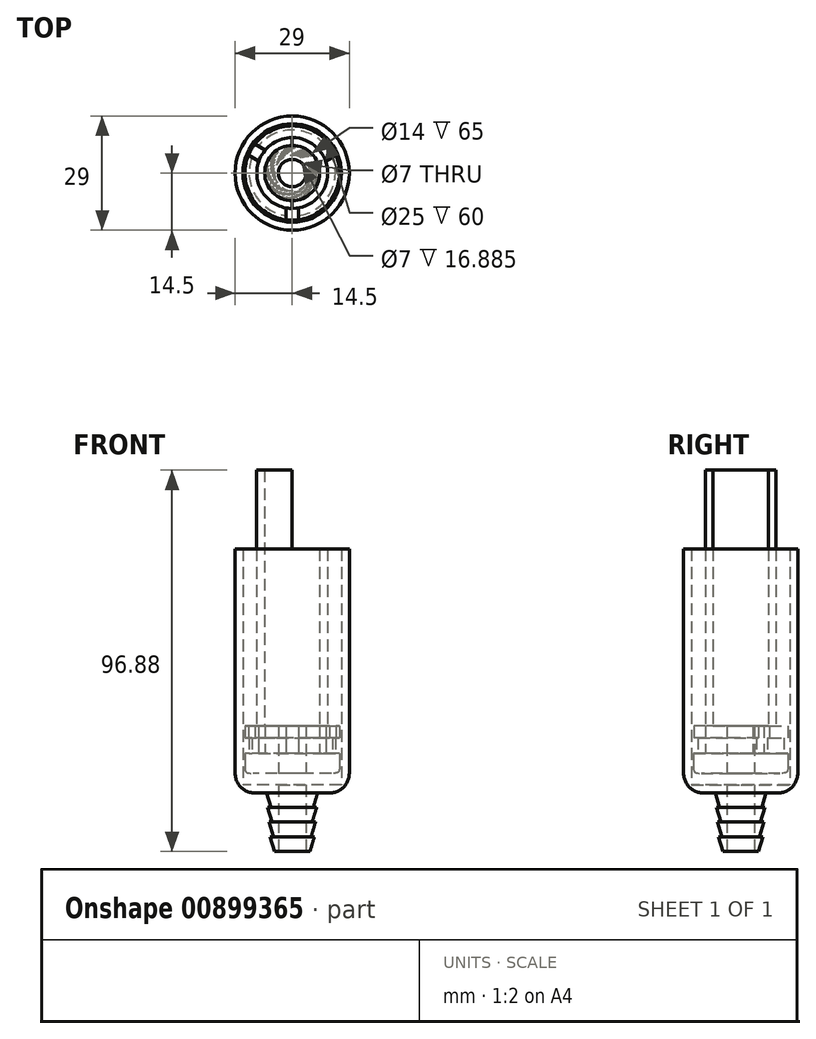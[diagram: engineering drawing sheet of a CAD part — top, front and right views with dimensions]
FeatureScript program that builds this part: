
annotation { "Feature Type Name" : "Feature", "Feature Type Description" : "" }
export const myFeature = defineFeature(function(context is Context, id is Id, definition is map)
    precondition{}
    {
        {
            var Q0;
            Q0=qCreatedBy(makeId("Top.planeOp"),FACE);
            var sketch = newSketch(context, id + "F0", { "sketchPlane" : qUnion([Q0])});
            skCircle(sketch, "E0", {"center": v(0, 0) * mm, "radius": 12 * mm});
            skSolve(sketch);
        }
        {
            var Q0;
            Q0=makeQuery(id+"F0.imprint","IMPRINT",FACE,{"disambiguationData":[TD([[makeQuery(id+"F0.imprint","IMPRINT",EDGE,{"derivedFrom":sQuery(id+"F0.wireOp",EDGE,"E0")}),1.0]])]});
            extrude(context, id + "F1", {"entities" : qUnion([Q0]), "depth" : 12 * mm, "offsetDistance" : 25 * mm});
        }
        {
            var Q0;
            Q0=makeQuery(id+"F1.opExtrude","CAP_FACE",FACE,{"disambiguationData":[OSD([sQuery(id+"F0.wireOp",EDGE,"E0")])],"isStart":false});
            var sketch = newSketch(context, id + "F2", { "sketchPlane" : qUnion([Q0])});
            skCircle(sketch, "E1", {"center": v(0, 0) * mm, "radius": 9 * mm});
            skCircle(sketch, "E2", {"center": v(0, 0) * mm, "radius": 7 * mm});
            skSolve(sketch);
        }
        {
            var Q0;
            Q0=makeQuery(id+"F2.imprint","IMPRINT",FACE,{"disambiguationData":[TD([[makeQuery(id+"F2.imprint","IMPRINT",EDGE,{"derivedFrom":sQuery(id+"F2.wireOp",EDGE,"E1")}),1.0]])]});
            extrude(context, id + "F3", {"entities" : qUnion([Q0]), "operationType" : NewBodyOperationType.ADD, "depth" : 65 * mm, "offsetDistance" : 25 * mm});
        }
        {
            var Q0;
            Q0=makeQuery(id+"F1.opExtrude","CAP_FACE",FACE,{"disambiguationData":[OSD([sQuery(id+"F0.wireOp",EDGE,"E0")])],"isStart":true});
            var sketch = newSketch(context, id + "F4", { "sketchPlane" : qUnion([Q0])});
            skLineSegment(sketch, "E3", {"start": v(8.06, 12) * mm, "end": v(-8.04, 12) * mm, "construction": true});
            skLineSegment(sketch, "E4", {"start": v(1.62, 8.93) * mm, "end": v(-1.62, 8.93) * mm});
            skPoint(sketch, "E5", {"position": v(0, 8.93) * mm});
            skLineSegment(sketch, "E6", {"start": v(1.62, 8.93) * mm, "end": v(1.62, 10.83) * mm});
            skLineSegment(sketch, "E7", {"start": v(-1.62, 8.93) * mm, "end": v(-1.62, 10.83) * mm});
            skLineSegment(sketch, "E8.1.0", {"start": v(-8.55, -3.06) * mm, "end": v(-6.92, -5.87) * mm});
            skPoint(sketch, "E8.1.1", {"position": v(-7.74, -4.47) * mm});
            skLineSegment(sketch, "E8.1.2", {"start": v(-6.92, -5.87) * mm, "end": v(-8.57, -6.82) * mm});
            skLineSegment(sketch, "E8.1.3", {"start": v(-8.55, -3.06) * mm, "end": v(-10.2, -4.01) * mm});
            skLineSegment(sketch, "E8.2.0", {"start": v(6.92, -5.87) * mm, "end": v(8.55, -3.06) * mm});
            skPoint(sketch, "E8.2.1", {"position": v(7.74, -4.47) * mm});
            skLineSegment(sketch, "E8.2.2", {"start": v(8.55, -3.06) * mm, "end": v(10.2, -4.01) * mm});
            skLineSegment(sketch, "E8.2.3", {"start": v(6.92, -5.87) * mm, "end": v(8.57, -6.82) * mm});
            skPoint(sketch, "E8.center", {"position": v(0, 0) * mm});
            skLineSegment(sketch, "E9", {"start": v(1.62, 10.83) * mm, "end": v(1.62, 10.83) * mm});
            skArc(sketch, "E10", {"start": v(-1.62, 10.83) * mm, "mid": v(0, -10.95) * mm, "end": v(1.62, 10.83) * mm});
            skArc(sketch, "E11", {"start": v(1.62, 10.83) * mm, "mid": v(0, 10.95) * mm, "end": v(-1.62, 10.83) * mm});
            skLineSegment(sketch, "E12", {"start": v(1.62, 10.83) * mm, "end": v(1.62, 11.89) * mm, "construction": true});
            skLineSegment(sketch, "E13", {"start": v(-1.62, 10.83) * mm, "end": v(-1.62, 11.89) * mm, "construction": true});
            skSolve(sketch);
        }
        {
            var Q0;
            Q0=makeQuery(id+"F4.imprint","IMPRINT",FACE,{"disambiguationData":[TD([[makeQuery(id+"F4.imprint","IMPRINT",EDGE,{"derivedFrom":makeQuery(id+"F1.opExtrude","CAP_EDGE",EDGE,{"disambiguationData":[OSD([sQuery(id+"F0.wireOp",EDGE,"E0")])],"isStart":true})}),-1.0]])]});
            extrude(context, id + "F5", {"entities" : qUnion([Q0]), "operationType" : NewBodyOperationType.REMOVE, "oppositeDirection" : true, "depth" : 9 * mm, "offsetDistance" : 25 * mm, "hasSecondDirection" : true, "secondDirectionOppositeDirection" : false, "secondDirectionDepth" : -5 * mm});
        }
        {
            var Q0;
            Q0=makeQuery(id+"F4.imprint","IMPRINT",FACE,{"disambiguationData":[TD([[makeQuery(id+"F4.imprint","IMPRINT",EDGE,{"derivedFrom":sQuery(id+"F4.wireOp",EDGE,"E4")}),-1.0]])]});
            var Q1;
            Q1=makeQuery(id+"F4.imprint","IMPRINT",FACE,{"disambiguationData":[TD([[makeQuery(id+"F4.imprint","IMPRINT",EDGE,{"derivedFrom":sQuery(id+"F4.wireOp",EDGE,"E8.1.0")}),-1.0]])]});
            var Q2;
            Q2=makeQuery(id+"F4.imprint","IMPRINT",FACE,{"disambiguationData":[TD([[makeQuery(id+"F4.imprint","IMPRINT",EDGE,{"derivedFrom":sQuery(id+"F4.wireOp",EDGE,"E8.2.0")}),-1.0]])]});
            var Q3;
            Q3=makeQuery(id+"F5.boolean.opBoolean","COPY",FACE,{"derivedFrom":makeQuery(id+"F5.opExtrude","CAP_FACE",FACE,{"disambiguationData":[OSD([sQuery(id+"F0.wireOp",EDGE,"E0"),sQuery(id+"F4.wireOp",EDGE,"bE9oeRPU-8ZHk-j5FX-hGk3-XUl1ZEH3Kncf")])],"isStart":false})});
            extrude(context, id + "F6", {"entities" : qUnion([Q0, Q1, Q2]), "operationType" : NewBodyOperationType.REMOVE, "endBound" : BoundingType.UP_TO_SURFACE, "oppositeDirection" : true, "depth" : 25 * mm, "endBoundEntityFace" : qUnion([Q3]), "offsetDistance" : 5 * mm, "hasSecondDirection" : true, "secondDirectionOppositeDirection" : true, "secondDirectionDepth" : 5 * mm});
        }
        {
            var Q0;
            {var subQ0=sQuery(id+"F4.wireOp",EDGE,"E10");var subQ1=sQuery(id+"F4.wireOp",EDGE,"E11");Q0=makeQuery(id+"F6.boolean.opBoolean","MERGE",FACE,{"derivedFrom":[makeQuery(id+"F5.boolean.opBoolean","COPY",FACE,{"derivedFrom":makeQuery(id+"F5.opExtrude","CAP_FACE",FACE,{"disambiguationData":[OSD([sQuery(id+"F0.wireOp",EDGE,"E0"),subQ0,subQ1])],"isStart":true})})],"fromTools":[makeQuery(id+"F6.opExtrude","CAP_FACE",FACE,{"disambiguationData":[OSD([sQuery(id+"F4.wireOp",EDGE,"E4"),sQuery(id+"F4.wireOp",EDGE,"E6"),sQuery(id+"F4.wireOp",EDGE,"E7"),subQ1])],"isStart":true}),makeQuery(id+"F6.opExtrude","CAP_FACE",FACE,{"disambiguationData":[OSD([sQuery(id+"F4.wireOp",EDGE,"E8.1.0"),sQuery(id+"F4.wireOp",EDGE,"E8.1.2"),sQuery(id+"F4.wireOp",EDGE,"E8.1.3"),subQ0])],"isStart":true}),makeQuery(id+"F6.opExtrude","CAP_FACE",FACE,{"disambiguationData":[OSD([sQuery(id+"F4.wireOp",EDGE,"E8.2.0"),sQuery(id+"F4.wireOp",EDGE,"E8.2.2"),sQuery(id+"F4.wireOp",EDGE,"E8.2.3"),subQ0])],"isStart":true})]});}
            var sketch = newSketch(context, id + "F7", { "sketchPlane" : qUnion([Q0])});
            skLineSegment(sketch, "E14", {"start": v(-1.62, -8.93) * mm, "end": v(-1.62, -11.89) * mm});
            skLineSegment(sketch, "E15", {"start": v(1.62, -8.93) * mm, "end": v(1.62, -11.89) * mm});
            skArc(sketch, "E16", {"start": v(-1.62, -11.89) * mm, "mid": v(0, -12) * mm, "end": v(1.62, -11.89) * mm});
            skPoint(sketch, "E17", {"position": v(0, -12) * mm});
            skPoint(sketch, "E18", {"position": v(0, -10.95) * mm});
            skLineSegment(sketch, "E19", {"start": v(1.62, -8.93) * mm, "end": v(-1.62, -8.93) * mm});
            skLineSegment(sketch, "E20.1.0", {"start": v(8.55, 3.06) * mm, "end": v(11.1, 4.54) * mm});
            skLineSegment(sketch, "E20.1.1", {"start": v(6.92, 5.87) * mm, "end": v(9.49, 7.35) * mm});
            skLineSegment(sketch, "E20.1.2", {"start": v(6.92, 5.87) * mm, "end": v(8.55, 3.06) * mm});
            skArc(sketch, "E20.1.3", {"start": v(11.1, 4.54) * mm, "mid": v(10.4, 6) * mm, "end": v(9.49, 7.35) * mm});
            skLineSegment(sketch, "E20.2.0", {"start": v(-6.92, 5.87) * mm, "end": v(-9.49, 7.35) * mm});
            skLineSegment(sketch, "E20.2.1", {"start": v(-8.55, 3.06) * mm, "end": v(-11.1, 4.54) * mm});
            skLineSegment(sketch, "E20.2.2", {"start": v(-8.55, 3.06) * mm, "end": v(-6.92, 5.87) * mm});
            skArc(sketch, "E20.2.3", {"start": v(-9.49, 7.35) * mm, "mid": v(-10.4, 6) * mm, "end": v(-11.1, 4.54) * mm});
            skSolve(sketch);
        }
        {
            var Q0;
            {var subQ15=sQuery(id+"F7.wireOp",EDGE,"E16");Q0=makeQuery(id+"F7.imprint","IMPRINT",FACE,{"disambiguationData":[TD([[makeQuery(id+"F7.imprint","IMPRINT",EDGE,{"derivedFrom":subQ15}),1.0]])]});}
            var Q1;
            {var subQ17=sQuery(id+"F7.wireOp",EDGE,"E20.2.2");Q1=makeQuery(id+"F7.imprint","IMPRINT",FACE,{"disambiguationData":[TD([[makeQuery(id+"F7.imprint","IMPRINT",EDGE,{"derivedFrom":subQ17}),1.0]])]});}
            var Q2;
            {var subQ17=sQuery(id+"F7.wireOp",EDGE,"E20.1.2");Q2=makeQuery(id+"F7.imprint","IMPRINT",FACE,{"disambiguationData":[TD([[makeQuery(id+"F7.imprint","IMPRINT",EDGE,{"derivedFrom":subQ17}),1.0]])]});}
            var Q3;
            {var subQ0=sQuery(id+"F0.wireOp",EDGE,"E0");Q3=makeQuery(id+"F3.boolean.opBoolean","SPLIT",FACE,{"disambiguationData":[TD([makeQuery(id+"F1.opExtrude","SWEPT_FACE",FACE,{"disambiguationData":[OSD([subQ0])]})])],"derivedFrom":makeQuery(id+"F1.opExtrude","CAP_FACE",FACE,{"disambiguationData":[OSD([subQ0])],"isStart":false})});}
            extrude(context, id + "F8", {"entities" : qUnion([Q0, Q1, Q2]), "operationType" : NewBodyOperationType.REMOVE, "endBound" : BoundingType.UP_TO_SURFACE, "depth" : 25 * mm, "endBoundEntityFace" : qUnion([Q3]), "offsetDistance" : 25 * mm});
        }
        {
            var Q0;
            Q0=makeQuery(id+"F1.opExtrude","CAP_EDGE",EDGE,{"disambiguationData":[OSD([sQuery(id+"F0.wireOp",EDGE,"E0")])],"isStart":true});
            fillet(context, id + "F9", {"entities" : qUnion([Q0]), "radius" : 2 * mm, "tangentPropagation" : true, "rho" : 0.7, "crossSection" : FilletCrossSection.CONIC, "allowEdgeOverflow" : false});
        }
        {
            var Q0;
            Q0=makeQuery(id+"F3.opExtrude","CAP_FACE",FACE,{"disambiguationData":[OSD([sQuery(id+"F2.wireOp",EDGE,"E1"),sQuery(id+"F2.wireOp",EDGE,"E2")])],"isStart":false});
            var sketch = newSketch(context, id + "F10", { "sketchPlane" : qUnion([Q0])});
            skLineSegment(sketch, "E21", {"start": v(0, 7) * mm, "end": v(0, 9) * mm});
            skLineSegment(sketch, "E22", {"start": v(0, -7) * mm, "end": v(0, -9) * mm});
            skArc(sketch, "E23", {"start": v(0, -7) * mm, "mid": v(7, 0) * mm, "end": v(0, 7) * mm});
            skArc(sketch, "E24", {"start": v(0, -9) * mm, "mid": v(9, 0) * mm, "end": v(0, 9) * mm});
            skSolve(sketch);
        }
        {
            var Q0;
            Q0=makeQuery(id+"F10.imprint","IMPRINT",FACE,{"disambiguationData":[TD([[makeQuery(id+"F10.imprint","IMPRINT",EDGE,{"derivedFrom":sQuery(id+"F10.wireOp",EDGE,"E21")}),-1.0]])]});
            extrude(context, id + "F11", {"entities" : qUnion([Q0]), "operationType" : NewBodyOperationType.REMOVE, "oppositeDirection" : true, "depth" : 20 * mm, "offsetDistance" : 25 * mm});
        }
        {
            var Q0;
            Q0=qCreatedBy(makeId("Top.planeOp"),FACE);
            var sketch = newSketch(context, id + "F12", { "sketchPlane" : qUnion([Q0])});
            skCircle(sketch, "E25.0", {"center": v(0, 0) * mm, "radius": 12 * mm, "construction": true});
            skCircle(sketch, "E26.0", {"center": v(0, 0) * mm, "radius": 12.5 * mm});
            skCircle(sketch, "E27.0", {"center": v(0, 0) * mm, "radius": 14.5 * mm});
            skSolve(sketch);
        }
        {
            var Q0;
            Q0=makeQuery(id+"F12.imprint","IMPRINT",FACE,{"disambiguationData":[TD([[makeQuery(id+"F12.imprint","IMPRINT",EDGE,{"derivedFrom":sQuery(id+"F12.wireOp",EDGE,"E26.0")}),-1.0]])]});
            var Q1;
            Q1=makeQuery(id+"F11.boolean.opBoolean","COPY",FACE,{"derivedFrom":makeQuery(id+"F11.opExtrude","CAP_FACE",FACE,{"disambiguationData":[OSD([sQuery(id+"F10.wireOp",EDGE,"E21"),sQuery(id+"F10.wireOp",EDGE,"E22"),sQuery(id+"F10.wireOp",EDGE,"E23"),sQuery(id+"F10.wireOp",EDGE,"E24")])],"isStart":false})});
            extrude(context, id + "F13", {"entities" : qUnion([Q0]), "endBound" : BoundingType.UP_TO_SURFACE, "depth" : 50 * mm, "endBoundEntityFace" : qUnion([Q1]), "offsetDistance" : 25 * mm, "hasSecondDirection" : true, "secondDirectionOppositeDirection" : true, "secondDirectionDepth" : 5 * mm});
        }
        {
            var Q0;
            Q0=makeQuery(id+"F13.opExtrude","CAP_FACE",FACE,{"disambiguationData":[OSD([sQuery(id+"F12.wireOp",EDGE,"E26.0"),sQuery(id+"F12.wireOp",EDGE,"E27.0")])],"isStart":true});
            var sketch = newSketch(context, id + "F14", { "sketchPlane" : qUnion([Q0])});
            skCircle(sketch, "E28.0", {"center": v(0, 0) * mm, "radius": 12.5 * mm});
            skSolve(sketch);
        }
        {
            var Q0;
            Q0=makeQuery(id+"F14.imprint","IMPRINT",FACE,{"disambiguationData":[TD([[makeQuery(id+"F14.imprint","IMPRINT",EDGE,{"derivedFrom":sQuery(id+"F14.wireOp",EDGE,"E28.0")}),-1.0]])]});
            extrude(context, id + "F15", {"entities" : qUnion([Q0]), "operationType" : NewBodyOperationType.ADD, "oppositeDirection" : true, "depth" : 2 * mm, "offsetDistance" : 25 * mm});
        }
        {
            var Q0;
            Q0=makeQuery(id+"F15.boolean.opBoolean","MERGE",FACE,{"derivedFrom":[makeQuery(id+"F13.opExtrude","CAP_FACE",FACE,{"disambiguationData":[OSD([sQuery(id+"F12.wireOp",EDGE,"E26.0"),sQuery(id+"F12.wireOp",EDGE,"E27.0")])],"isStart":true}),makeQuery(id+"F15.opExtrude","CAP_FACE",FACE,{"disambiguationData":[OSD([sQuery(id+"F14.wireOp",EDGE,"E28.0")])],"isStart":true})]});
            var sketch = newSketch(context, id + "F16", { "sketchPlane" : qUnion([Q0])});
            skCircle(sketch, "E29", {"center": v(0, 0) * mm, "radius": 3.5 * mm});
            skCircle(sketch, "E30.0", {"center": v(0, 0) * mm, "radius": 5.5 * mm});
            skSolve(sketch);
        }
        {
            var Q0;
            Q0=qCreatedBy(makeId("Right.planeOp"),FACE);
            var sketch = newSketch(context, id + "F17", { "sketchPlane" : qUnion([Q0])});
            skLineSegment(sketch, "E31", {"start": v(0, -4.88) * mm, "end": v(-6.5, -4.88) * mm});
            skLineSegment(sketch, "E32", {"start": v(-6.5, -4.88) * mm, "end": v(-5.35, -19.88) * mm, "construction": true});
            skLineSegment(sketch, "E33", {"start": v(-6.5, -4.88) * mm, "end": v(-5.36, -8.63) * mm});
            skLineSegment(sketch, "E34", {"start": v(-5.36, -8.63) * mm, "end": v(-6.21, -8.63) * mm});
            skLineSegment(sketch, "E35", {"start": v(-6.21, -8.63) * mm, "end": v(-5.07, -12.38) * mm});
            skLineSegment(sketch, "E36", {"start": v(-5.07, -12.38) * mm, "end": v(-5.93, -12.38) * mm});
            skLineSegment(sketch, "E37", {"start": v(-5.93, -12.38) * mm, "end": v(-4.79, -16.13) * mm});
            skLineSegment(sketch, "E38", {"start": v(-4.79, -16.13) * mm, "end": v(-5.64, -16.13) * mm});
            skLineSegment(sketch, "E39", {"start": v(-5.64, -16.13) * mm, "end": v(-4.5, -19.88) * mm});
            skLineSegment(sketch, "E40", {"start": v(-5.35, -19.88) * mm, "end": v(-4.5, -19.88) * mm, "construction": true});
            skLineSegment(sketch, "E41", {"start": v(0, -4.88) * mm, "end": v(0, -19.88) * mm});
            skLineSegment(sketch, "E42", {"start": v(-4.5, -19.88) * mm, "end": v(0, -19.88) * mm});
            skSolve(sketch);
        }
        {
            var Q0;
            Q0=makeQuery(id+"F17.imprint","IMPRINT",FACE,{"disambiguationData":[TD([[makeQuery(id+"F17.imprint","IMPRINT",EDGE,{"derivedFrom":sQuery(id+"F17.wireOp",EDGE,"E31")}),1.0]])]});
            var Q1;
            Q1=sQuery(id+"F17.wireOp",EDGE,"E41");
            revolve(context, id + "F18", {"operationType" : NewBodyOperationType.ADD, "surfaceOperationType" : NewSurfaceOperationType.NEW, "entities" : qUnion([Q0]), "axis" : qUnion([Q1]), "revolveType" : RevolveType.FULL});
        }
        {
            var Q0;
            Q0=makeQuery(id+"F4.imprint","IMPRINT",FACE,{"disambiguationData":[TD([[makeQuery(id+"F4.imprint","IMPRINT",EDGE,{"derivedFrom":sQuery(id+"F4.wireOp",EDGE,"E4")}),1.0]])]});
            var sketch = newSketch(context, id + "F19", { "sketchPlane" : qUnion([Q0])});
            skCircle(sketch, "E43.0", {"center": v(0, 0) * mm, "radius": 3.5 * mm});
            skSolve(sketch);
        }
        {
            var Q0;
            Q0=makeQuery(id+"F19.imprint","IMPRINT",FACE,{"disambiguationData":[TD([[makeQuery(id+"F19.imprint","IMPRINT",EDGE,{"derivedFrom":sQuery(id+"F19.wireOp",EDGE,"E43.0")}),1.0]])]});
            var Q1;
            Q1=makeQuery(id+"F18.opRevolve","SWEPT_FACE",FACE,{"disambiguationData":[OSD([sQuery(id+"F17.wireOp",EDGE,"E42")])]});
            extrude(context, id + "F20", {"entities" : qUnion([Q0]), "operationType" : NewBodyOperationType.REMOVE, "endBound" : BoundingType.UP_TO_NEXT, "oppositeDirection" : true, "depth" : 25 * mm, "offsetDistance" : 25 * mm, "hasSecondDirection" : true, "secondDirectionBound" : SecondDirectionBoundingType.UP_TO_SURFACE, "secondDirectionOppositeDirection" : false, "secondDirectionDepth" : 25 * mm, "secondDirectionBoundEntityFace" : qUnion([Q1])});
        }
        {
            var Q0;
            Q0=makeQuery(id+"F13.opExtrude","CAP_EDGE",EDGE,{"disambiguationData":[OSD([sQuery(id+"F12.wireOp",EDGE,"E27.0")])],"isStart":true});
            fillet(context, id + "F21", {"entities" : qUnion([Q0]), "radius" : 5 * mm, "tangentPropagation" : true, "allowEdgeOverflow" : false});
        }
    });
